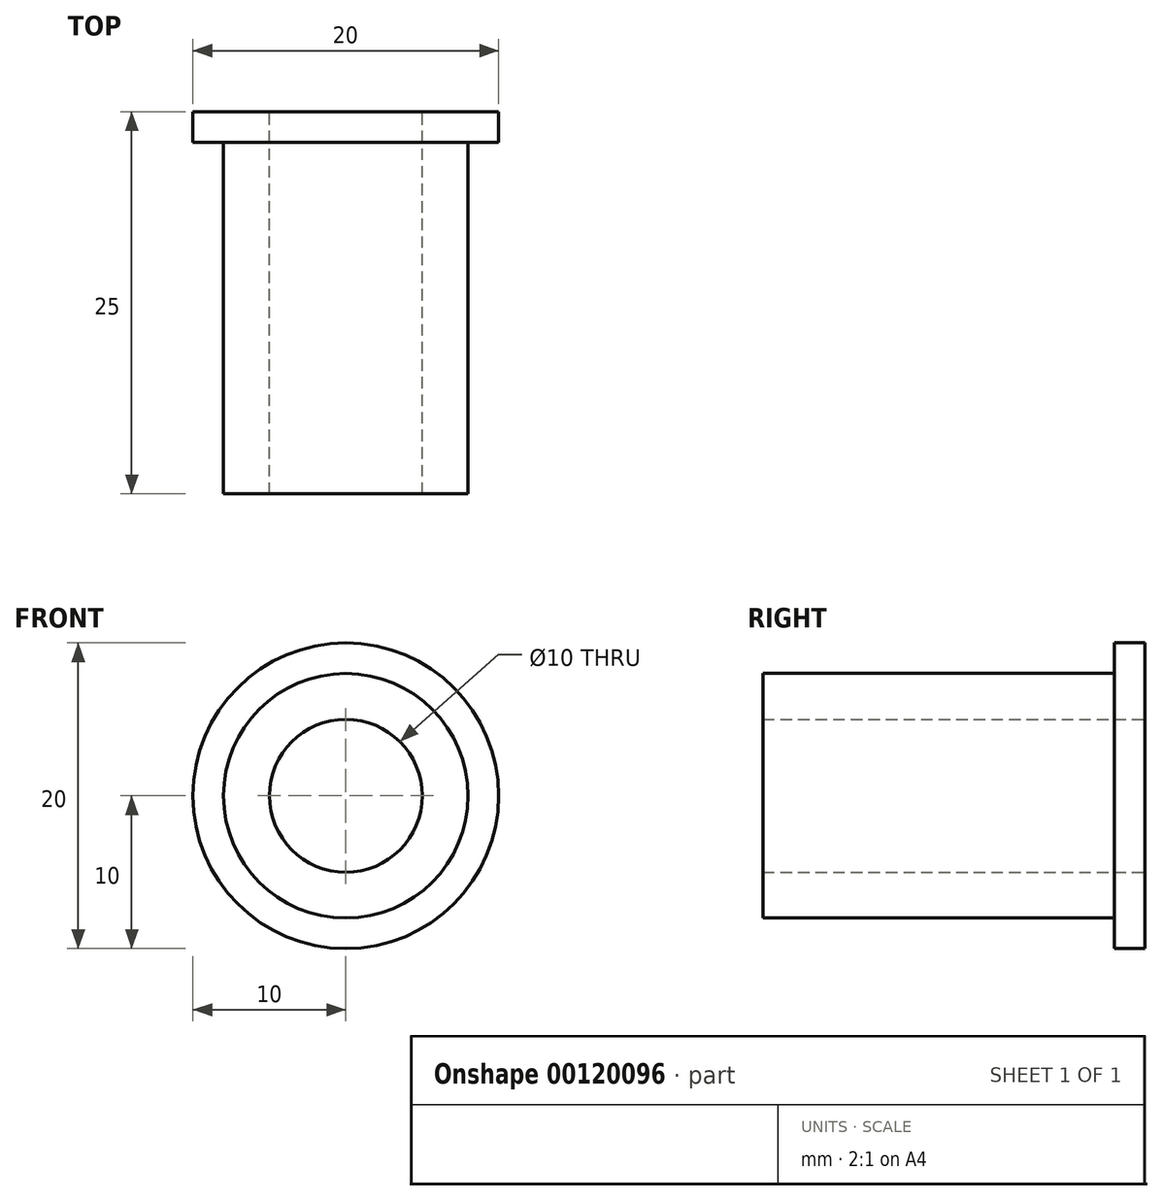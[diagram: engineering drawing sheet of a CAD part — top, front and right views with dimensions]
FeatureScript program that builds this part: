
annotation { "Feature Type Name" : "Feature", "Feature Type Description" : "" }
export const myFeature = defineFeature(function(context is Context, id is Id, definition is map)
    precondition{}
    {
        {
            var Q0;
            Q0=qCreatedBy(makeId("Front.planeOp"),FACE);
            var sketch = newSketch(context, id + "F0", { "sketchPlane" : qUnion([Q0])});
            skCircle(sketch, "E0", {"center": v(0, 0) * mm, "radius": 5 * mm});
            skCircle(sketch, "E1", {"center": v(0, 0) * mm, "radius": 8 * mm});
            skSolve(sketch);
        }
        {
            var Q0;
            Q0=makeQuery(id+"F0.imprint","IMPRINT",FACE,{"disambiguationData":[TD([[makeQuery(id+"F0.imprint","IMPRINT",EDGE,{"derivedFrom":sQuery(id+"F0.wireOp",EDGE,"E0")}),-1.0]])]});
            extrude(context, id + "F1", {"entities" : qUnion([Q0]), "endBound" : BoundingType.SYMMETRIC, "depth" : 23 * mm});
        }
        {
            var Q0;
            Q0=makeQuery(id+"F1.opExtrude","CAP_FACE",FACE,{"disambiguationData":[OSD([sQuery(id+"F0.wireOp",EDGE,"E0"),sQuery(id+"F0.wireOp",EDGE,"E1")])],"isStart":true});
            var sketch = newSketch(context, id + "F2", { "sketchPlane" : qUnion([Q0])});
            skCircle(sketch, "E2", {"center": v(0, 0) * mm, "radius": 10 * mm});
            skSolve(sketch);
        }
        {
            var Q0;
            Q0=makeQuery(id+"F2.imprint","IMPRINT",FACE,{"disambiguationData":[TD([[makeQuery(id+"F2.imprint","IMPRINT",EDGE,{"derivedFrom":sQuery(id+"F2.wireOp",EDGE,"E2")}),1.0]])]});
            var Q1;
            Q1=makeQuery(id+"F2.imprint","IMPRINT",FACE,{"disambiguationData":[TD([[makeQuery(id+"F2.imprint","IMPRINT",EDGE,{"derivedFrom":makeQuery(id+"F1.opExtrude","CAP_EDGE",EDGE,{"disambiguationData":[OSD([sQuery(id+"F0.wireOp",EDGE,"E0")])],"isStart":true})}),1.0]])]});
            extrude(context, id + "F3", {"entities" : qUnion([Q0, Q1]), "operationType" : NewBodyOperationType.ADD, "depth" : 2 * mm});
        }
    });
